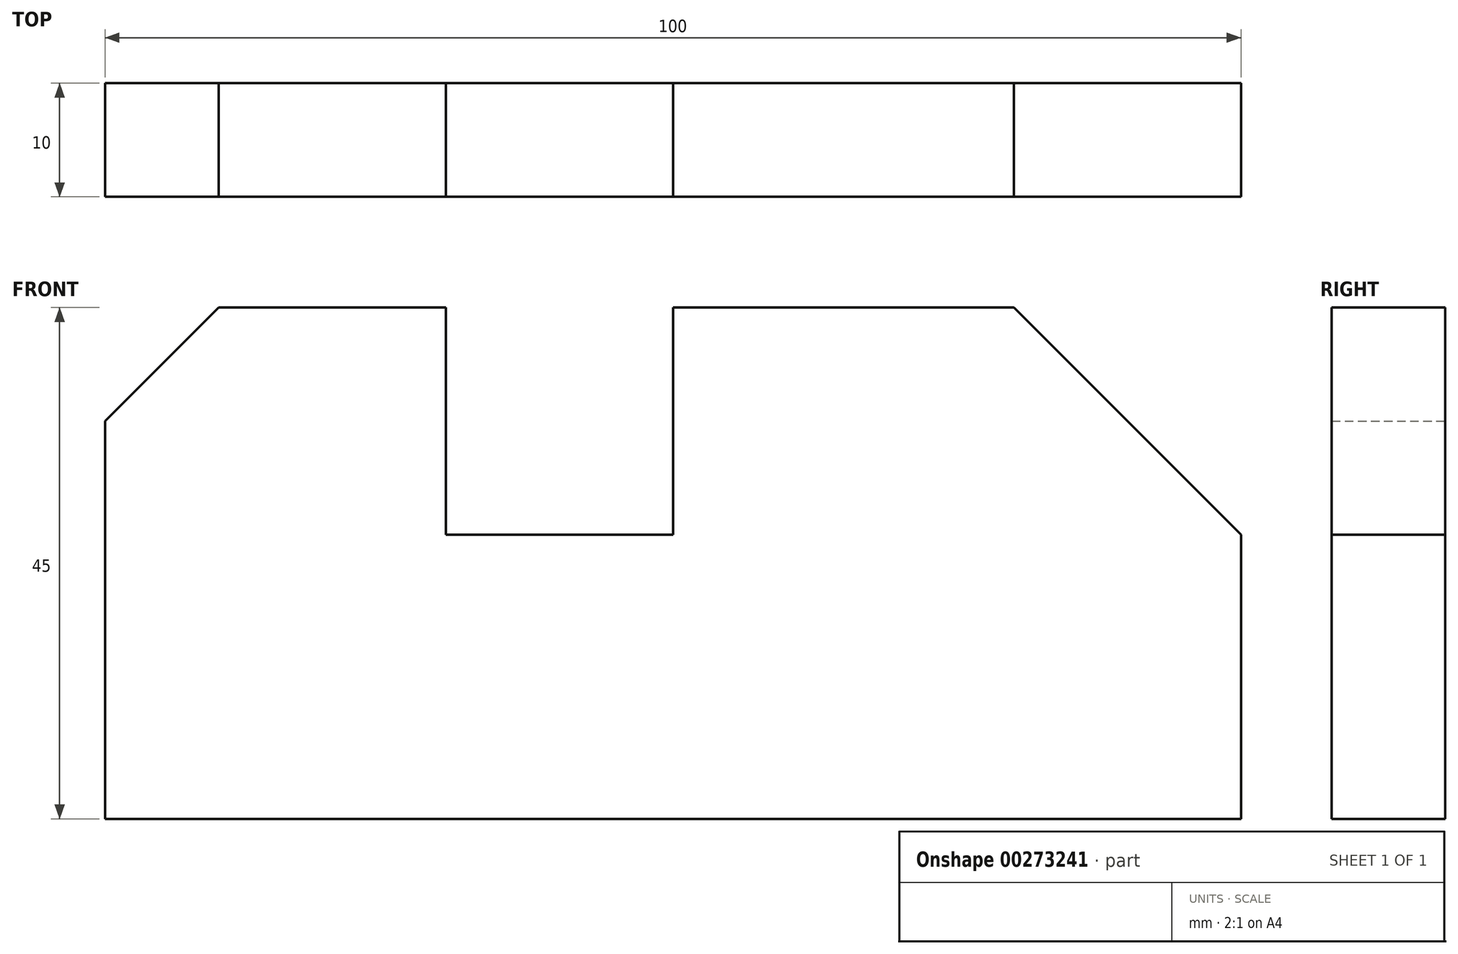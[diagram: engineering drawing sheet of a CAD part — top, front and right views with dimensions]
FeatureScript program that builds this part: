
annotation { "Feature Type Name" : "Feature", "Feature Type Description" : "" }
export const myFeature = defineFeature(function(context is Context, id is Id, definition is map)
    precondition{}
    {
        {
            var Q0;
            Q0=qCreatedBy(makeId("Front.planeOp"),FACE);
            var sketch = newSketch(context, id + "F0", { "sketchPlane" : qUnion([Q0])});
            skLineSegment(sketch, "E0", {"start": v(0, 0) * mm, "end": v(100, 0) * mm});
            skLineSegment(sketch, "E1", {"start": v(0, 0) * mm, "end": v(0, 35) * mm});
            skLineSegment(sketch, "E2", {"start": v(0, 35) * mm, "end": v(10, 45) * mm});
            skLineSegment(sketch, "E3", {"start": v(10, 45) * mm, "end": v(30, 45) * mm});
            skLineSegment(sketch, "E4", {"start": v(30, 45) * mm, "end": v(30, 25) * mm});
            skLineSegment(sketch, "E5", {"start": v(30, 25) * mm, "end": v(50, 25) * mm});
            skLineSegment(sketch, "E6", {"start": v(50, 25) * mm, "end": v(50, 45) * mm});
            skLineSegment(sketch, "E7", {"start": v(100, 0) * mm, "end": v(100, 25) * mm});
            skLineSegment(sketch, "E8", {"start": v(50, 45) * mm, "end": v(80, 45) * mm});
            skLineSegment(sketch, "E9", {"start": v(100, 25) * mm, "end": v(80, 45) * mm});
            skSolve(sketch);
        }
        {
            var Q0;
            Q0 = qSketchRegion(id + "F0", true);
            extrude(context, id + "F1", {"entities" : qUnion([Q0]), "depth" : 10 * mm});
        }
    });
